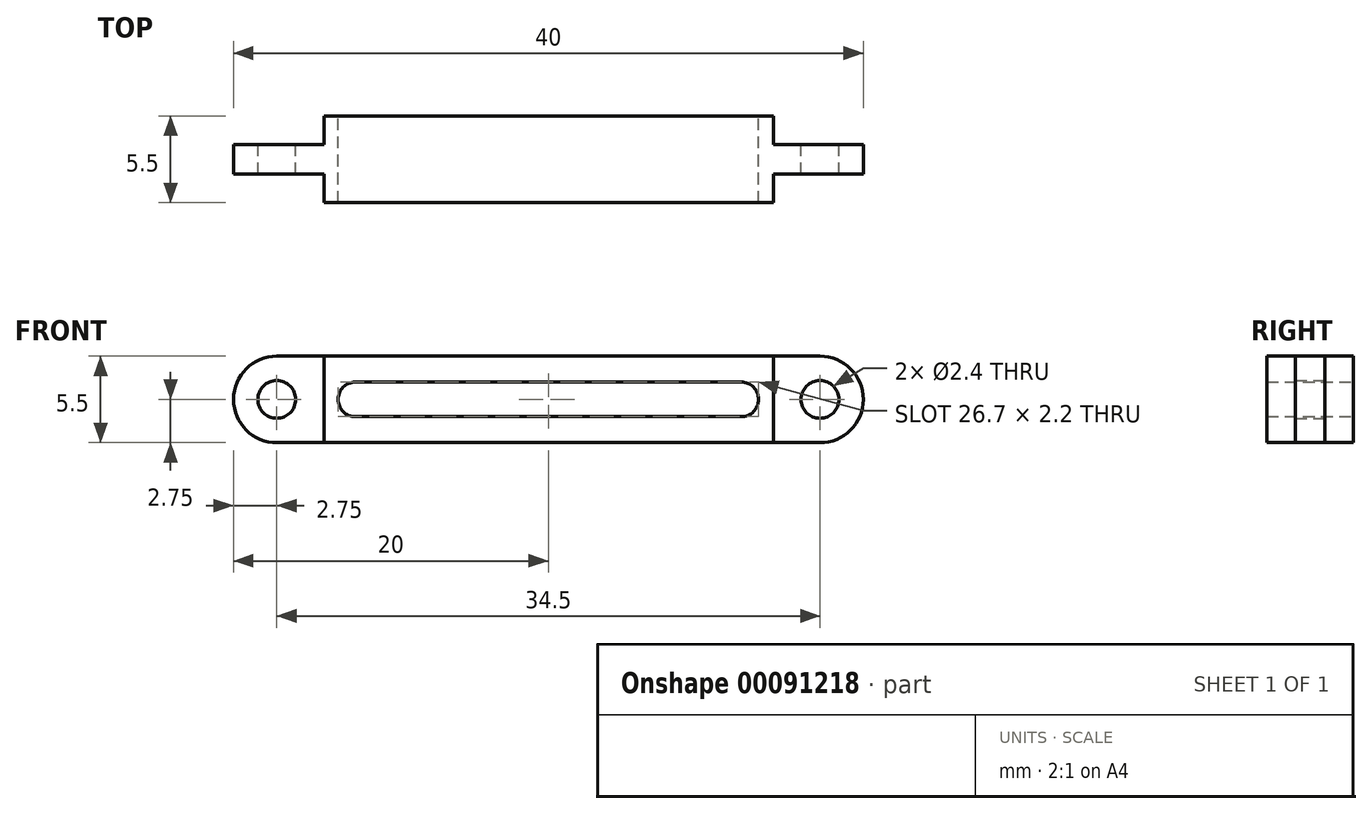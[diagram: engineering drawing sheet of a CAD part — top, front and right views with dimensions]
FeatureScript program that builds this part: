
annotation { "Feature Type Name" : "Feature", "Feature Type Description" : "" }
export const myFeature = defineFeature(function(context is Context, id is Id, definition is map)
    precondition{}
    {
        {
            var Q0;
            Q0=qCreatedBy(makeId("Front.planeOp"),FACE);
            var sketch = newSketch(context, id + "F0", { "sketchPlane" : qUnion([Q0])});
            skLineSegment(sketch, "E0.bottom", {"start": v(0, 0) * mm, "end": v(40, 0) * mm});
            skLineSegment(sketch, "E0.top", {"start": v(0, 5.5) * mm, "end": v(40, 5.5) * mm});
            skLineSegment(sketch, "E0.left", {"start": v(0, 0) * mm, "end": v(0, 5.5) * mm});
            skLineSegment(sketch, "E0.right", {"start": v(40, 0) * mm, "end": v(40, 5.5) * mm});
            skSolve(sketch);
        }
        {
            var Q0;
            Q0=makeQuery(id+"F0.imprint","IMPRINT",FACE,{"disambiguationData":[TD([[makeQuery(id+"F0.imprint","IMPRINT",EDGE,{"derivedFrom":sQuery(id+"F0.wireOp",EDGE,"E0.bottom")}),1.0]])]});
            extrude(context, id + "F1", {"entities" : qUnion([Q0]), "depth" : 5.5 * mm});
        }
        {
            var Q0;
            Q0=makeQuery(id+"F1.opExtrude","SWEPT_EDGE",EDGE,{"disambiguationData":[OSD([sQuery(id+"F0.wireOp",EDGE,"E0.top"),sQuery(id+"F0.wireOp",EDGE,"E0.left")])]});
            var Q1;
            Q1=makeQuery(id+"F1.opExtrude","SWEPT_EDGE",EDGE,{"disambiguationData":[OSD([sQuery(id+"F0.wireOp",EDGE,"E0.top"),sQuery(id+"F0.wireOp",EDGE,"E0.right")])]});
            var Q2;
            Q2=makeQuery(id+"F1.opExtrude","SWEPT_EDGE",EDGE,{"disambiguationData":[OSD([sQuery(id+"F0.wireOp",EDGE,"E0.bottom"),sQuery(id+"F0.wireOp",EDGE,"E0.right")])]});
            var Q3;
            Q3=makeQuery(id+"F1.opExtrude","SWEPT_EDGE",EDGE,{"disambiguationData":[OSD([sQuery(id+"F0.wireOp",EDGE,"E0.bottom"),sQuery(id+"F0.wireOp",EDGE,"E0.left")])]});
            fillet(context, id + "F2", {"entities" : qUnion([Q0, Q1, Q2, Q3]), "radius" : 2.75 * mm, "tangentPropagation" : true, "allowEdgeOverflow" : false});
        }
        {
            var Q0;
            Q0=makeQuery(id+"F1.opExtrude","SWEPT_FACE",FACE,{"disambiguationData":[OSD([sQuery(id+"F0.wireOp",EDGE,"E0.top")])]});
            var sketch = newSketch(context, id + "F3", { "sketchPlane" : qUnion([Q0])});
            skLineSegment(sketch, "E1.bottom", {"start": v(34.3, -1.8) * mm, "end": v(40.1, -1.8) * mm});
            skLineSegment(sketch, "E1.top", {"start": v(34.3, 0) * mm, "end": v(40.1, 0) * mm});
            skLineSegment(sketch, "E1.left", {"start": v(34.3, -1.8) * mm, "end": v(34.3, 0) * mm});
            skLineSegment(sketch, "E1.right", {"start": v(40.1, -1.8) * mm, "end": v(40.1, 0) * mm});
            skLineSegment(sketch, "E2.bottom", {"start": v(34.3, -3.7) * mm, "end": v(40.1, -3.7) * mm});
            skLineSegment(sketch, "E2.top", {"start": v(34.3, -5.5) * mm, "end": v(40.1, -5.5) * mm});
            skLineSegment(sketch, "E2.left", {"start": v(34.3, -3.7) * mm, "end": v(34.3, -5.5) * mm});
            skLineSegment(sketch, "E2.right", {"start": v(40.1, -3.7) * mm, "end": v(40.1, -5.5) * mm});
            skSolve(sketch);
        }
        {
            var Q0;
            {var subQ0=sQuery(id+"F3.wireOp",EDGE,"E1.left");Q0=makeQuery(id+"F3.imprint","IMPRINT",FACE,{"disambiguationData":[TD([[makeQuery(id+"F3.imprint","IMPRINT",EDGE,{"derivedFrom":subQ0}),-1.0]])]});}
            var Q1;
            {var subQ0=sQuery(id+"F3.wireOp",EDGE,"E1.right");Q1=makeQuery(id+"F3.imprint","IMPRINT",FACE,{"disambiguationData":[TD([[makeQuery(id+"F3.imprint","IMPRINT",EDGE,{"derivedFrom":subQ0}),1.0]])]});}
            var Q2;
            {var subQ0=sQuery(id+"F3.wireOp",EDGE,"E2.right");Q2=makeQuery(id+"F3.imprint","IMPRINT",FACE,{"disambiguationData":[TD([[makeQuery(id+"F3.imprint","IMPRINT",EDGE,{"derivedFrom":subQ0}),-1.0]])]});}
            var Q3;
            {var subQ0=sQuery(id+"F3.wireOp",EDGE,"E2.left");Q3=makeQuery(id+"F3.imprint","IMPRINT",FACE,{"disambiguationData":[TD([[makeQuery(id+"F3.imprint","IMPRINT",EDGE,{"derivedFrom":subQ0}),1.0]])]});}
            extrude(context, id + "F4", {"entities" : qUnion([Q0, Q1, Q2, Q3]), "operationType" : NewBodyOperationType.REMOVE, "endBound" : BoundingType.THROUGH_ALL, "oppositeDirection" : true, "depth" : 25 * mm});
        }
        {
            var Q0;
            Q0=makeQuery(id+"F1.opExtrude","SWEPT_FACE",FACE,{"disambiguationData":[OSD([sQuery(id+"F0.wireOp",EDGE,"E0.top")])]});
            var sketch = newSketch(context, id + "F5", { "sketchPlane" : qUnion([Q0])});
            skLineSegment(sketch, "E3.bottom", {"start": v(5.75, 0) * mm, "end": v(0, 0) * mm});
            skLineSegment(sketch, "E3.top", {"start": v(5.75, -1.8) * mm, "end": v(0, -1.8) * mm});
            skLineSegment(sketch, "E3.left", {"start": v(5.75, 0) * mm, "end": v(5.75, -1.8) * mm});
            skLineSegment(sketch, "E3.right", {"start": v(0, 0) * mm, "end": v(0, -1.8) * mm});
            skLineSegment(sketch, "E4.bottom", {"start": v(5.75, -5.5) * mm, "end": v(0, -5.5) * mm});
            skLineSegment(sketch, "E4.top", {"start": v(5.75, -3.7) * mm, "end": v(0, -3.7) * mm});
            skLineSegment(sketch, "E4.left", {"start": v(5.75, -5.5) * mm, "end": v(5.75, -3.7) * mm});
            skLineSegment(sketch, "E4.right", {"start": v(0, -5.5) * mm, "end": v(0, -3.7) * mm});
            skSolve(sketch);
        }
        {
            var Q0;
            {var subQ4=sQuery(id+"F5.wireOp",EDGE,"E3.left");Q0=makeQuery(id+"F5.imprint","IMPRINT",FACE,{"disambiguationData":[TD([[makeQuery(id+"F5.imprint","IMPRINT",EDGE,{"derivedFrom":subQ4}),-1.0]])]});}
            var Q1;
            {var subQ4=sQuery(id+"F5.wireOp",EDGE,"E3.right");Q1=makeQuery(id+"F5.imprint","IMPRINT",FACE,{"disambiguationData":[TD([[makeQuery(id+"F5.imprint","IMPRINT",EDGE,{"derivedFrom":subQ4}),1.0]])]});}
            var Q2;
            {var subQ4=sQuery(id+"F5.wireOp",EDGE,"E4.right");Q2=makeQuery(id+"F5.imprint","IMPRINT",FACE,{"disambiguationData":[TD([[makeQuery(id+"F5.imprint","IMPRINT",EDGE,{"derivedFrom":subQ4}),-1.0]])]});}
            var Q3;
            {var subQ4=sQuery(id+"F5.wireOp",EDGE,"E4.left");Q3=makeQuery(id+"F5.imprint","IMPRINT",FACE,{"disambiguationData":[TD([[makeQuery(id+"F5.imprint","IMPRINT",EDGE,{"derivedFrom":subQ4}),1.0]])]});}
            extrude(context, id + "F6", {"entities" : qUnion([Q0, Q1, Q2, Q3]), "operationType" : NewBodyOperationType.REMOVE, "endBound" : BoundingType.THROUGH_ALL, "oppositeDirection" : true, "depth" : 25 * mm});
        }
        {
            var Q0;
            Q0=makeQuery(id+"F6.boolean.opBoolean","COPY",FACE,{"derivedFrom":makeQuery(id+"F6.opExtrude","SWEPT_FACE",FACE,{"disambiguationData":[OSD([sQuery(id+"F5.wireOp",EDGE,"E3.top")])]})});
            var sketch = newSketch(context, id + "F7", { "sketchPlane" : qUnion([Q0])});
            skCircle(sketch, "E5", {"center": v(-2.75, 2.75) * mm, "radius": 1.2 * mm});
            skSolve(sketch);
        }
        {
            var Q0;
            Q0=makeQuery(id+"F7.imprint","IMPRINT",FACE,{"disambiguationData":[TD([[makeQuery(id+"F7.imprint","IMPRINT",EDGE,{"derivedFrom":sQuery(id+"F7.wireOp",EDGE,"E5")}),1.0]])]});
            extrude(context, id + "F8", {"entities" : qUnion([Q0]), "operationType" : NewBodyOperationType.REMOVE, "endBound" : BoundingType.THROUGH_ALL, "oppositeDirection" : true, "depth" : 25 * mm});
        }
        {
            var Q0;
            Q0=makeQuery(id+"F4.boolean.opBoolean","COPY",FACE,{"derivedFrom":makeQuery(id+"F4.opExtrude","SWEPT_FACE",FACE,{"disambiguationData":[OSD([sQuery(id+"F3.wireOp",EDGE,"E1.bottom")])]})});
            var sketch = newSketch(context, id + "F9", { "sketchPlane" : qUnion([Q0])});
            skCircle(sketch, "E6", {"center": v(-37.25, 2.75) * mm, "radius": 1.2 * mm});
            skSolve(sketch);
        }
        {
            var Q0;
            Q0=makeQuery(id+"F9.imprint","IMPRINT",FACE,{"disambiguationData":[TD([[makeQuery(id+"F9.imprint","IMPRINT",EDGE,{"derivedFrom":sQuery(id+"F9.wireOp",EDGE,"E6")}),1.0]])]});
            extrude(context, id + "F10", {"entities" : qUnion([Q0]), "operationType" : NewBodyOperationType.REMOVE, "endBound" : BoundingType.THROUGH_ALL, "oppositeDirection" : true, "depth" : 25 * mm});
        }
        {
            var Q0;
            Q0=makeQuery(id+"F1.opExtrude","CAP_FACE",FACE,{"disambiguationData":[OSD([sQuery(id+"F0.wireOp",EDGE,"E0.bottom"),sQuery(id+"F0.wireOp",EDGE,"E0.top"),sQuery(id+"F0.wireOp",EDGE,"E0.left"),sQuery(id+"F0.wireOp",EDGE,"E0.right")])],"isStart":true});
            var sketch = newSketch(context, id + "F11", { "sketchPlane" : qUnion([Q0])});
            skSolve(sketch);
        }
        {
            var Q0;
            Q0=makeQuery(id+"F11.imprint","IMPRINT",FACE,{"disambiguationData":[TD([[makeQuery(id+"F11.imprint","IMPRINT",EDGE,{"derivedFrom":makeQuery(id+"F1.opExtrude","CAP_EDGE",EDGE,{"disambiguationData":[OSD([sQuery(id+"F0.wireOp",EDGE,"E0.bottom")])],"isStart":true})}),-1.0]])]});
            var sketch = newSketch(context, id + "F12", { "sketchPlane" : qUnion([Q0])});
            skLineSegment(sketch, "E7", {"start": v(-7.75, 1.65) * mm, "end": v(-32.25, 1.65) * mm});
            skLineSegment(sketch, "E8", {"start": v(-7.75, 3.85) * mm, "end": v(-32.25, 3.85) * mm});
            skArc(sketch, "E9", {"start": v(-7.75, 1.65) * mm, "mid": v(-6.65, 2.75) * mm, "end": v(-7.75, 3.85) * mm});
            skArc(sketch, "E10", {"start": v(-32.25, 3.85) * mm, "mid": v(-33.35, 2.75) * mm, "end": v(-32.25, 1.65) * mm});
            skSolve(sketch);
        }
        {
            var Q0;
            Q0=makeQuery(id+"F12.imprint","IMPRINT",FACE,{"disambiguationData":[TD([[makeQuery(id+"F12.imprint","IMPRINT",EDGE,{"derivedFrom":sQuery(id+"F12.wireOp",EDGE,"E7")}),-1.0]])]});
            var Q1;
            Q1 = qSketchRegion(id + "F11", true);
            extrude(context, id + "F13", {"entities" : qUnion([Q0, Q1]), "operationType" : NewBodyOperationType.REMOVE, "endBound" : BoundingType.THROUGH_ALL, "oppositeDirection" : true, "depth" : 25 * mm});
        }
    });
